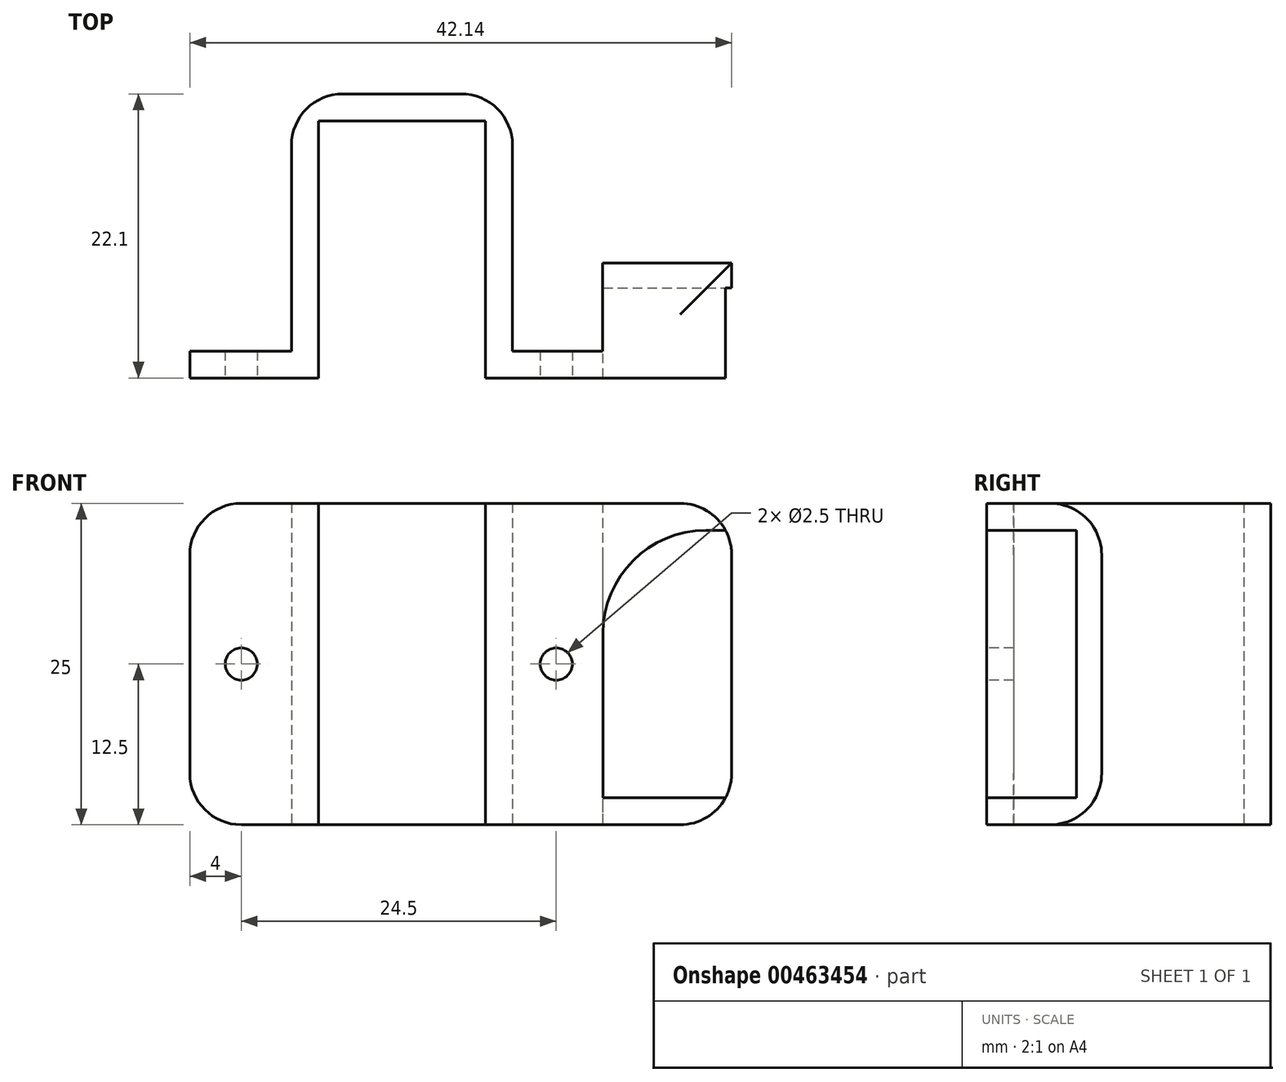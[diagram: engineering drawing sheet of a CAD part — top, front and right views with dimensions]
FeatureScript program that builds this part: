
annotation { "Feature Type Name" : "Feature", "Feature Type Description" : "" }
export const myFeature = defineFeature(function(context is Context, id is Id, definition is map)
    precondition{}
    {
        {
            var Q0;
            Q0=qCreatedBy(makeId("Top.planeOp"),FACE);
            var sketch = newSketch(context, id + "F0", { "sketchPlane" : qUnion([Q0])});
            skLineSegment(sketch, "E0", {"start": v(0, 0) * mm, "end": v(0, 20) * mm});
            skLineSegment(sketch, "E1", {"start": v(0, 20) * mm, "end": v(-13, 20) * mm});
            skLineSegment(sketch, "E2", {"start": v(-13, 20) * mm, "end": v(-13, 0) * mm});
            skLineSegment(sketch, "E3", {"start": v(-13, 0) * mm, "end": v(-23, 0) * mm});
            skLineSegment(sketch, "E4", {"start": v(-23, 0) * mm, "end": v(-23, 2.1) * mm});
            skLineSegment(sketch, "E5", {"start": v(-23, 2.1) * mm, "end": v(-15.1, 2.1) * mm});
            skLineSegment(sketch, "E6", {"start": v(-15.1, 2.1) * mm, "end": v(-15.1, 22.1) * mm});
            skLineSegment(sketch, "E7", {"start": v(-15.1, 22.1) * mm, "end": v(2.1, 22.1) * mm});
            skLineSegment(sketch, "E8", {"start": v(2.1, 22.1) * mm, "end": v(2.1, 2.1) * mm});
            skLineSegment(sketch, "E9", {"start": v(2.1, 2.1) * mm, "end": v(9.1, 2.1) * mm});
            skLineSegment(sketch, "E10", {"start": v(9.1, 2.1) * mm, "end": v(9.1, 0) * mm});
            skLineSegment(sketch, "E11", {"start": v(9.1, 0) * mm, "end": v(0, 0) * mm});
            skLineSegment(sketch, "E12", {"start": v(9.1, 2.1) * mm, "end": v(9.1, 8.95) * mm});
            skLineSegment(sketch, "E13", {"start": v(9.1, 8.95) * mm, "end": v(19.14, 8.95) * mm});
            skLineSegment(sketch, "E14", {"start": v(19.14, 8.95) * mm, "end": v(19.14, 0) * mm});
            skLineSegment(sketch, "E15", {"start": v(19.14, 0) * mm, "end": v(9.1, 0) * mm});
            skSolve(sketch);
        }
        {
            var Q0;
            Q0 = qSketchRegion(id + "F0", true);
            extrude(context, id + "F1", {"entities" : qUnion([Q0]), "depth" : 25 * mm});
        }
        {
            var Q0;
            Q0=makeQuery(id+"F1.opExtrude","SWEPT_FACE",FACE,{"disambiguationData":[OSD([sQuery(id+"F0.wireOp",EDGE,"E14")])]});
            cPlane(context, id + "F2", {"entities" : qUnion([Q0]), "cplaneType" : CPlaneType.OFFSET, "offset" : 0 * mm, "width" : 150 * mm, "height" : 150 * mm});
        }
        {
            var Q0;
            Q0=qCreatedBy(id+"F2.planeOp",FACE);
            var sketch = newSketch(context, id + "F3", { "sketchPlane" : qUnion([Q0])});
            skLineSegment(sketch, "E16", {"start": v(0, 0) * mm, "end": v(0, 2.1) * mm});
            skLineSegment(sketch, "E17", {"start": v(0, 2.1) * mm, "end": v(7, 2.1) * mm});
            skLineSegment(sketch, "E18", {"start": v(7, 2.1) * mm, "end": v(7, 22.9) * mm});
            skLineSegment(sketch, "E19", {"start": v(7, 22.9) * mm, "end": v(0, 22.9) * mm});
            skLineSegment(sketch, "E20", {"start": v(0, 22.9) * mm, "end": v(0, 2.1) * mm});
            skSolve(sketch);
        }
        {
            var Q0;
            Q0 = qSketchRegion(id + "F3", true);
            extrude(context, id + "F4", {"entities" : qUnion([Q0]), "operationType" : NewBodyOperationType.REMOVE, "oppositeDirection" : true, "depth" : 10 * mm});
        }
        {
            var Q0;
            Q0=qCreatedBy(makeId("Front.planeOp"),FACE);
            var sketch = newSketch(context, id + "F5", { "sketchPlane" : qUnion([Q0])});
            skLineSegment(sketch, "E21", {"start": v(0, 0) * mm, "end": v(0, 12.5) * mm, "construction": true});
            skLineSegment(sketch, "E22", {"start": v(0, 12.5) * mm, "end": v(-19, 12.5) * mm, "construction": true});
            skLineSegment(sketch, "E23", {"start": v(0, 12.5) * mm, "end": v(5.5, 12.5) * mm, "construction": true});
            skCircle(sketch, "E24", {"center": v(-19, 12.5) * mm, "radius": 1.25 * mm});
            skCircle(sketch, "E25", {"center": v(5.5, 12.5) * mm, "radius": 1.25 * mm});
            skSolve(sketch);
        }
        {
            var Q0;
            Q0 = qSketchRegion(id + "F5", true);
            extrude(context, id + "F6", {"entities" : qUnion([Q0]), "operationType" : NewBodyOperationType.REMOVE, "oppositeDirection" : true, "depth" : 25 * mm});
        }
        {
            var Q0;
            Q0=makeQuery(id+"F1.opExtrude","SWEPT_EDGE",EDGE,{"disambiguationData":[OSD([sQuery(id+"F0.wireOp",EDGE,"E6"),sQuery(id+"F0.wireOp",EDGE,"E7")])]});
            var Q1;
            Q1=makeQuery(id+"F1.opExtrude","SWEPT_EDGE",EDGE,{"disambiguationData":[OSD([sQuery(id+"F0.wireOp",EDGE,"E7"),sQuery(id+"F0.wireOp",EDGE,"E8")])]});
            var Q2;
            Q2=makeQuery(id+"F1.opExtrude","CAP_EDGE",EDGE,{"disambiguationData":[OSD([sQuery(id+"F0.wireOp",EDGE,"E13")])],"isStart":false});
            var Q3;
            Q3=makeQuery(id+"F1.opExtrude","CAP_EDGE",EDGE,{"disambiguationData":[OSD([sQuery(id+"F0.wireOp",EDGE,"E13")])],"isStart":true});
            var Q4;
            Q4=makeQuery(id+"F1.opExtrude","CAP_EDGE",EDGE,{"disambiguationData":[OSD([sQuery(id+"F0.wireOp",EDGE,"E4")])],"isStart":false});
            var Q5;
            Q5=makeQuery(id+"F1.opExtrude","CAP_EDGE",EDGE,{"disambiguationData":[OSD([sQuery(id+"F0.wireOp",EDGE,"E4")])],"isStart":true});
            var Q6;
            Q6=makeQuery(id+"F1.opExtrude","CAP_EDGE",EDGE,{"disambiguationData":[OSD([sQuery(id+"F0.wireOp",EDGE,"E14")])],"isStart":false});
            var Q7;
            Q7=makeQuery(id+"F1.opExtrude","CAP_EDGE",EDGE,{"disambiguationData":[OSD([sQuery(id+"F0.wireOp",EDGE,"E14")])],"isStart":true});
            fillet(context, id + "F7", {"entities" : qUnion([Q0, Q1, Q2, Q3, Q4, Q5, Q6, Q7]), "radius" : 4 * mm, "tangentPropagation" : true, "allowEdgeOverflow" : false});
        }
        {
            var Q0;
            Q0=makeQuery(id+"F4.boolean.opBoolean","COPY",EDGE,{"derivedFrom":makeQuery(id+"F4.opExtrude","CAP_EDGE",EDGE,{"disambiguationData":[OSD([sQuery(id+"F3.wireOp",EDGE,"E19")])],"isStart":false})});
            fillet(context, id + "F8", {"entities" : qUnion([Q0]), "radius" : 8 * mm, "tangentPropagation" : true, "allowEdgeOverflow" : false});
        }
    });
